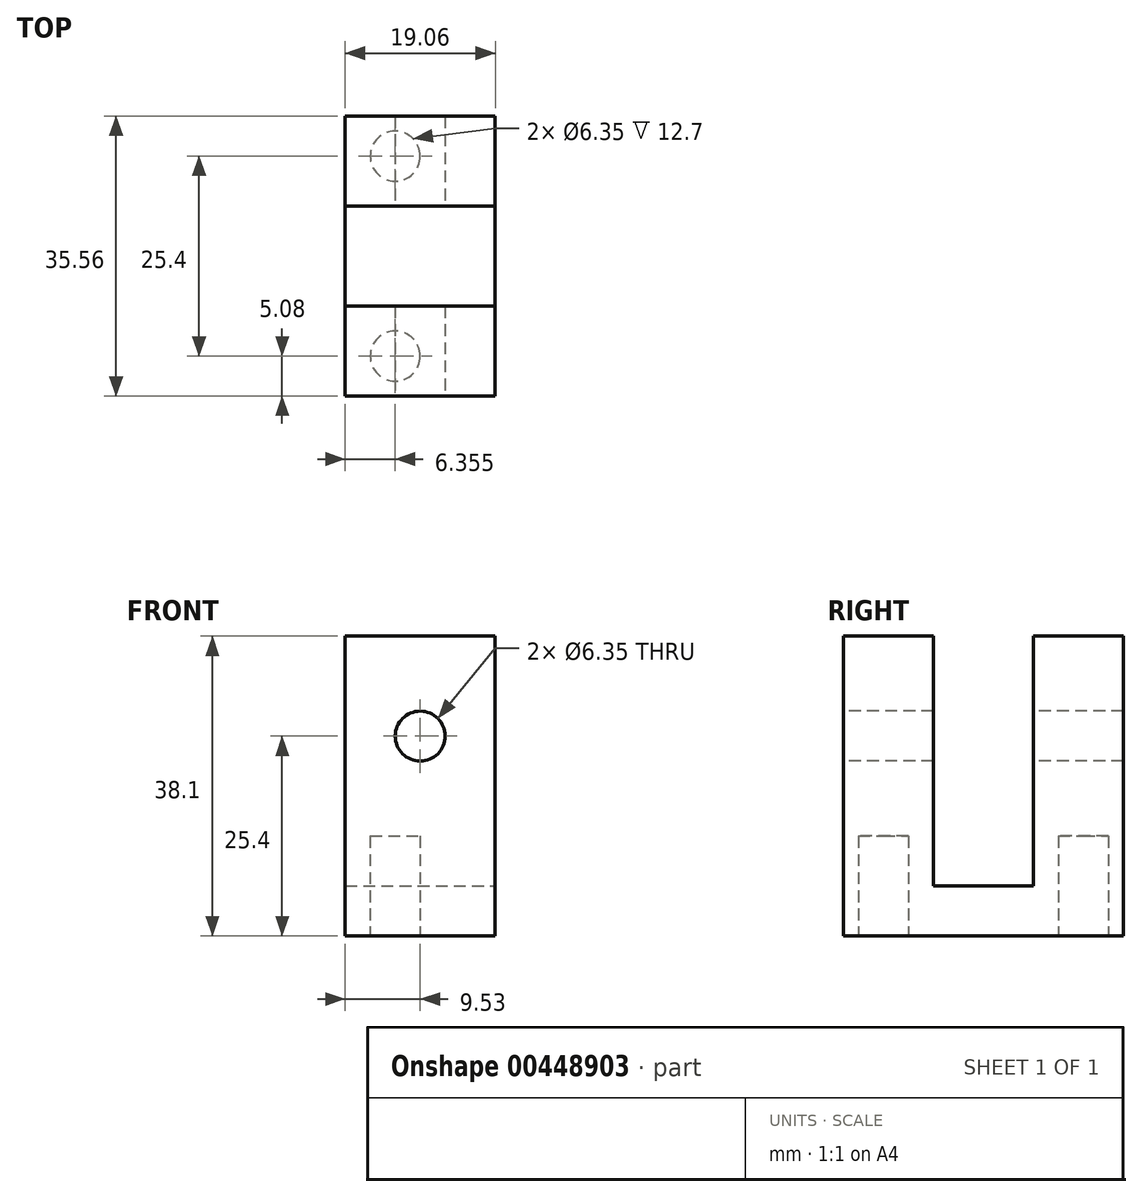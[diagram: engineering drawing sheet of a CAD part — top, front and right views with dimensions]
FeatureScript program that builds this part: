
annotation { "Feature Type Name" : "Feature", "Feature Type Description" : "" }
export const myFeature = defineFeature(function(context is Context, id is Id, definition is map)
    precondition{}
    {
        {
            var Q0;
            Q0=qCreatedBy(makeId("Front.planeOp"),FACE);
            var sketch = newSketch(context, id + "F0", { "sketchPlane" : qUnion([Q0])});
            skLineSegment(sketch, "E0.bottom", {"start": v(-9.52, 38.1) * mm, "end": v(9.52, 38.1) * mm});
            skLineSegment(sketch, "E0.top", {"start": v(-9.52, 0) * mm, "end": v(9.52, 0) * mm});
            skLineSegment(sketch, "E0.left", {"start": v(-9.52, 38.1) * mm, "end": v(-9.52, 0) * mm});
            skLineSegment(sketch, "E0.right", {"start": v(9.53, 38.1) * mm, "end": v(9.53, 0) * mm});
            skSolve(sketch);
        }
        {
            var Q0;
            Q0 = qSketchRegion(id + "F0", true);
            extrude(context, id + "F1", {"entities" : qUnion([Q0]), "endBound" : BoundingType.SYMMETRIC, "depth" : 35.56 * mm});
        }
        {
            var Q0;
            Q0=qCreatedBy(makeId("Right.planeOp"),FACE);
            var sketch = newSketch(context, id + "F2", { "sketchPlane" : qUnion([Q0])});
            skLineSegment(sketch, "E1.bottom", {"start": v(-6.35, 38.1) * mm, "end": v(6.35, 38.1) * mm});
            skLineSegment(sketch, "E1.top", {"start": v(-6.35, 6.35) * mm, "end": v(6.35, 6.35) * mm});
            skLineSegment(sketch, "E1.left", {"start": v(-6.35, 38.1) * mm, "end": v(-6.35, 6.35) * mm});
            skLineSegment(sketch, "E1.right", {"start": v(6.35, 38.1) * mm, "end": v(6.35, 6.35) * mm});
            skSolve(sketch);
        }
        {
            var Q0;
            Q0 = qSketchRegion(id + "F2", true);
            extrude(context, id + "F3", {"entities" : qUnion([Q0]), "operationType" : NewBodyOperationType.REMOVE, "endBound" : BoundingType.SYMMETRIC, "oppositeDirection" : true, "depth" : 19.05 * mm});
        }
        {
            var Q0;
            Q0=makeQuery(id+"F1.opExtrude","CAP_FACE",FACE,{"disambiguationData":[OSD([sQuery(id+"F0.wireOp",EDGE,"E0.bottom"),sQuery(id+"F0.wireOp",EDGE,"E0.top"),sQuery(id+"F0.wireOp",EDGE,"E0.left"),sQuery(id+"F0.wireOp",EDGE,"E0.right")])],"isStart":false});
            var sketch = newSketch(context, id + "F4", { "sketchPlane" : qUnion([Q0])});
            skCircle(sketch, "E2", {"center": v(0, 25.4) * mm, "radius": 3.18 * mm});
            skSolve(sketch);
        }
        {
            var Q0;
            Q0 = qSketchRegion(id + "F4", true);
            extrude(context, id + "F5", {"entities" : qUnion([Q0]), "operationType" : NewBodyOperationType.REMOVE, "endBound" : BoundingType.THROUGH_ALL, "oppositeDirection" : true, "depth" : 25.4 * mm});
        }
        {
            var Q0;
            Q0=makeQuery(id+"F1.opExtrude","SWEPT_FACE",FACE,{"disambiguationData":[OSD([sQuery(id+"F0.wireOp",EDGE,"E0.top")])]});
            var sketch = newSketch(context, id + "F6", { "sketchPlane" : qUnion([Q0])});
            skCircle(sketch, "E3", {"center": v(-3.17, 12.7) * mm, "radius": 3.17 * mm});
            skCircle(sketch, "E4", {"center": v(-3.17, -12.7) * mm, "radius": 3.17 * mm});
            skSolve(sketch);
        }
        {
            var Q0;
            Q0 = qSketchRegion(id + "F6", true);
            extrude(context, id + "F7", {"entities" : qUnion([Q0]), "operationType" : NewBodyOperationType.REMOVE, "oppositeDirection" : true, "depth" : 12.7 * mm});
        }
    });
